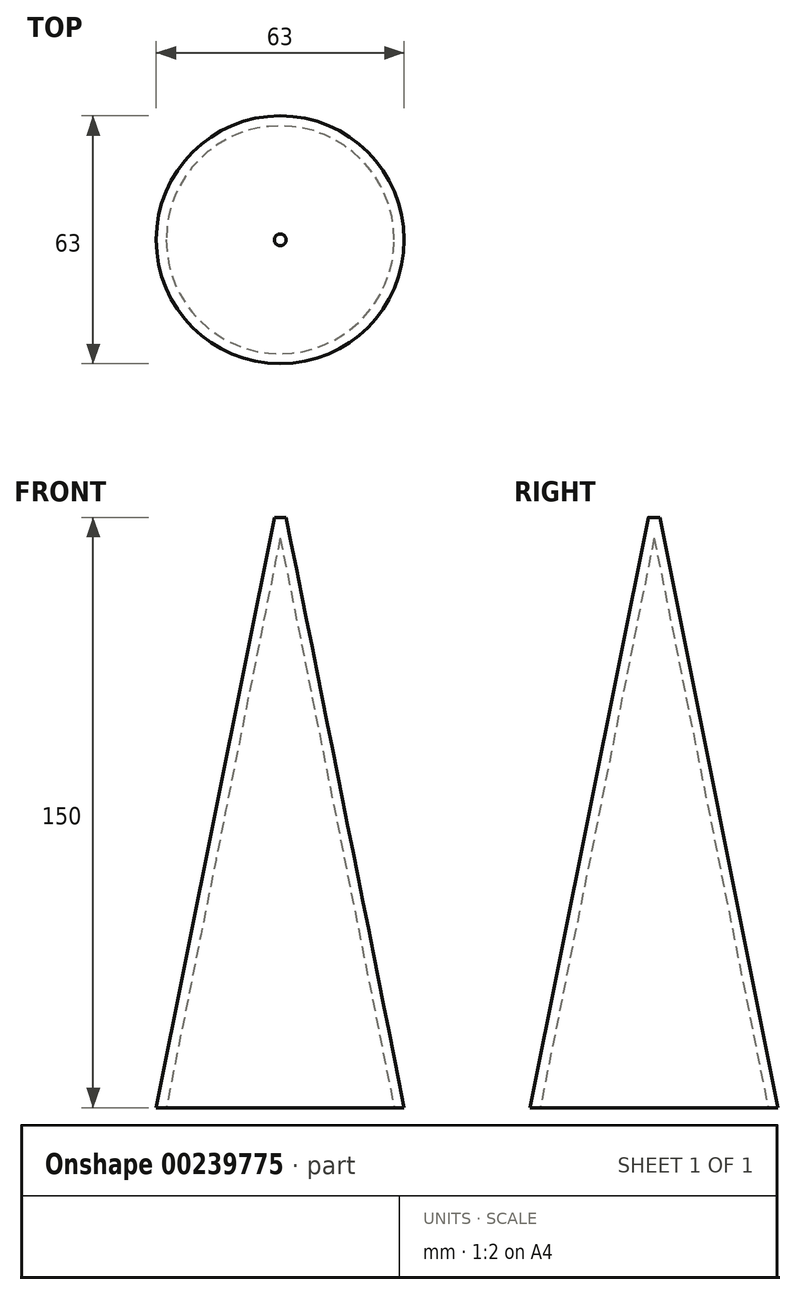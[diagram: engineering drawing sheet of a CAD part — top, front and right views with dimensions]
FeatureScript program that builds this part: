
annotation { "Feature Type Name" : "Feature", "Feature Type Description" : "" }
export const myFeature = defineFeature(function(context is Context, id is Id, definition is map)
    precondition{}
    {
        {
            var Q0;
            Q0=qCreatedBy(makeId("Top.planeOp"),FACE);
            var sketch = newSketch(context, id + "F0", { "sketchPlane" : qUnion([Q0])});
            skCircle(sketch, "E0", {"center": v(0, 0) * mm, "radius": 31.5 * mm});
            skSolve(sketch);
        }
        {
            var Q0;
            Q0 = qSketchRegion(id + "F0", true);
            extrude(context, id + "F1", {"entities" : qUnion([Q0]), "depth" : 150 * mm});
        }
        {
            var Q0;
            Q0=makeQuery(id+"F1.opExtrude","CAP_EDGE",EDGE,{"disambiguationData":[OSD([sQuery(id+"F0.wireOp",EDGE,"E0")])],"isStart":false});
            chamfer(context, id + "F2", {"entities" : qUnion([Q0]), "chamferType" : ChamferType.TWO_OFFSETS, "width1" : 30 * mm, "oppositeDirection" : false, "width2" : 150 * mm, "tangentPropagation" : true});
        }
        {
            var Q0;
            Q0=makeQuery(id+"F1.opExtrude","CAP_FACE",FACE,{"disambiguationData":[OSD([sQuery(id+"F0.wireOp",EDGE,"E0")])],"isStart":true});
            shell(context, id + "F3", {"entities" : qUnion([Q0]), "thickness" : 2.5 * mm});
        }
    });
